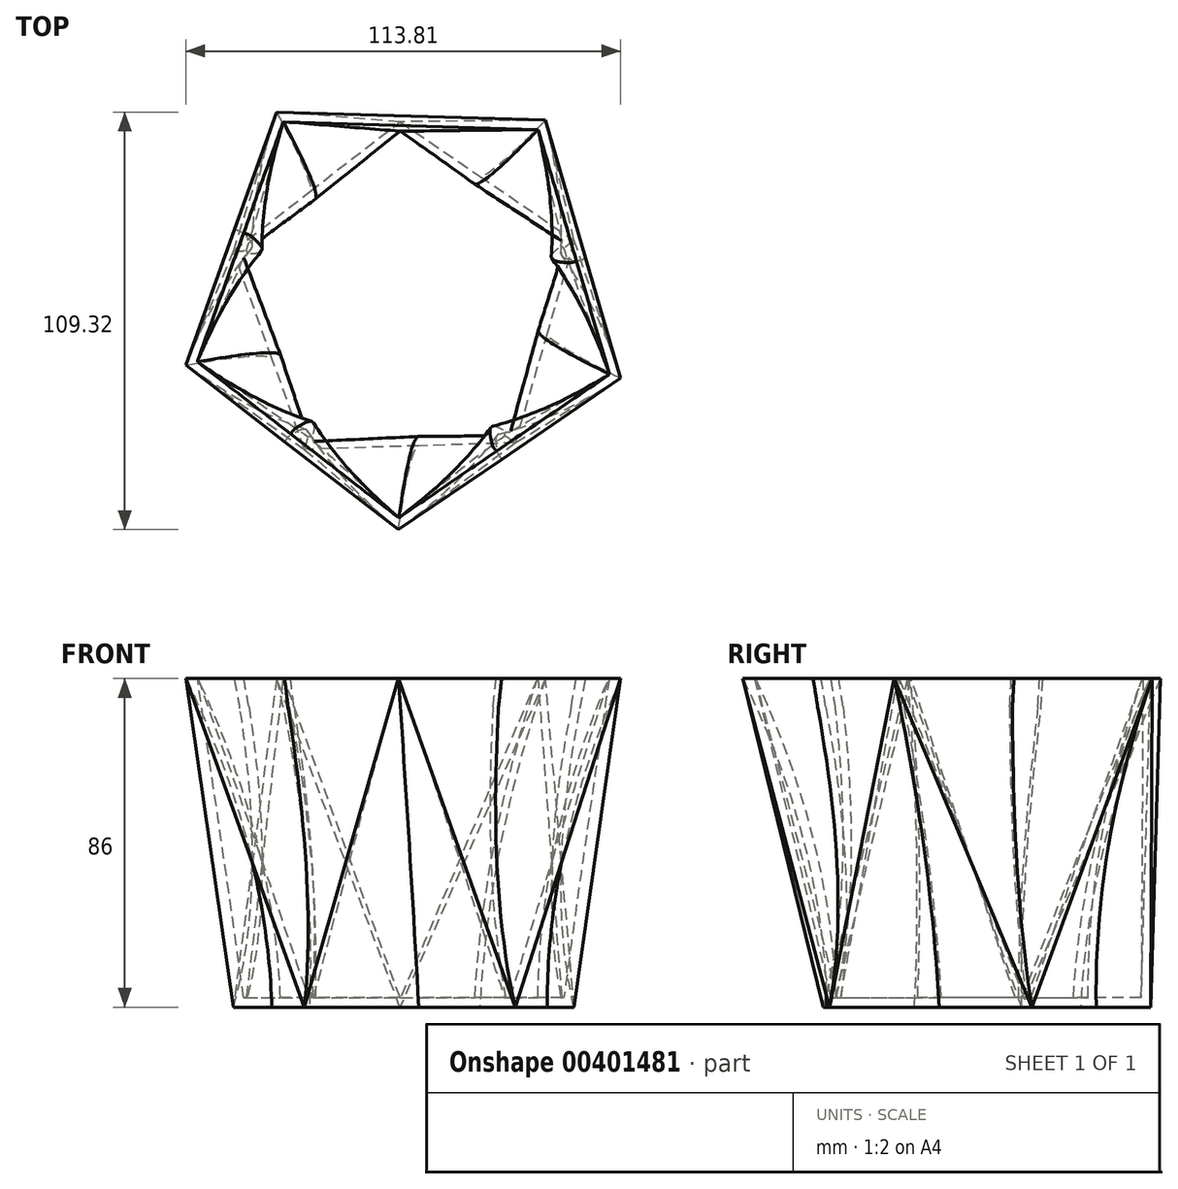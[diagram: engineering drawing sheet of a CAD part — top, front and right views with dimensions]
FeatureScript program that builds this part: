
annotation { "Feature Type Name" : "Feature", "Feature Type Description" : "" }
export const myFeature = defineFeature(function(context is Context, id is Id, definition is map)
    precondition{}
    {
        {
            var Q0;
            Q0=qCreatedBy(makeId("Top.planeOp"),FACE);
            var sketch = newSketch(context, id + "F0", { "sketchPlane" : qUnion([Q0])});
            skCircle(sketch, "E0.cCircle", {"center": v(0, 0) * mm, "radius": 37.98 * mm, "construction": true});
            skLineSegment(sketch, "E0.0", {"start": v(-1.43, 46.92) * mm, "end": v(44.18, 15.86) * mm});
            skLineSegment(sketch, "E0.1", {"start": v(44.18, 15.86) * mm, "end": v(28.73, -37.12) * mm});
            skLineSegment(sketch, "E0.2", {"start": v(28.73, -37.12) * mm, "end": v(-26.42, -38.8) * mm});
            skLineSegment(sketch, "E0.3", {"start": v(-26.42, -38.8) * mm, "end": v(-45.06, 13.14) * mm});
            skLineSegment(sketch, "E0.4", {"start": v(-45.06, 13.14) * mm, "end": v(-1.43, 46.92) * mm});
            skPoint(sketch, "E0.0.midPoint", {"position": v(21.38, 31.39) * mm});
            skSolve(sketch);
        }
        {
            var Q0;
            Q0=qCreatedBy(makeId("Top.planeOp"),FACE);
            cPlane(context, id + "F1", {"entities" : qUnion([Q0]), "cplaneType" : CPlaneType.OFFSET, "offset" : 86 * mm, "width" : 150 * mm, "height" : 150 * mm});
        }
        {
            var Q0;
            Q0=qCreatedBy(id+"F1.planeOp",FACE);
            var sketch = newSketch(context, id + "F2", { "sketchPlane" : qUnion([Q0])});
            skCircle(sketch, "E1.cCircle", {"center": v(0, 0) * mm, "radius": 48.43 * mm, "construction": true});
            skLineSegment(sketch, "E1.0", {"start": v(36.65, 47.34) * mm, "end": v(56.34, -20.23) * mm});
            skLineSegment(sketch, "E1.1", {"start": v(56.34, -20.23) * mm, "end": v(-1.82, -59.84) * mm});
            skLineSegment(sketch, "E1.2", {"start": v(-1.82, -59.84) * mm, "end": v(-57.47, -16.75) * mm});
            skLineSegment(sketch, "E1.3", {"start": v(-57.47, -16.75) * mm, "end": v(-33.7, 49.48) * mm});
            skLineSegment(sketch, "E1.4", {"start": v(-33.7, 49.48) * mm, "end": v(36.65, 47.34) * mm});
            skPoint(sketch, "E1.0.midPoint", {"position": v(46.5, 13.55) * mm});
            skSolve(sketch);
        }
        {
            var Q0;
            Q0=makeQuery(id+"F0.imprint","IMPRINT",FACE,{"disambiguationData":[TD([[makeQuery(id+"F0.imprint","IMPRINT",EDGE,{"derivedFrom":sQuery(id+"F0.wireOp",EDGE,"E0.0")}),-1.0]])]});
            var Q1;
            Q1=makeQuery(id+"F2.imprint","IMPRINT",FACE,{"disambiguationData":[TD([[makeQuery(id+"F2.imprint","IMPRINT",EDGE,{"derivedFrom":sQuery(id+"F2.wireOp",EDGE,"E1.0")}),-1.0]])]});
            loft(context, id + "F3", {"sheetProfilesArray" : [{ "sheetProfileEntities" : qUnion([Q0]) }, { "sheetProfileEntities" : qUnion([Q1]) }]});
        }
        {
            var Q1;
            Q1=makeQuery(id+"F3.opLoft","CAP_FACE",FACE,{"disambiguationData":[OSD([makeQuery(id+"F2.imprint","IMPRINT",FACE,{"disambiguationData":[TD([[makeQuery(id+"F2.imprint","IMPRINT",EDGE,{"derivedFrom":sQuery(id+"F2.wireOp",EDGE,"E1.0")}),-1.0]])]})])],"isStart":true});
            var Q2;
            Q2=makeQuery(id+"F3.opLoft","CAP_FACE",FACE,{"disambiguationData":[OSD([makeQuery(id+"F0.imprint","IMPRINT",FACE,{"disambiguationData":[TD([[makeQuery(id+"F0.imprint","IMPRINT",EDGE,{"derivedFrom":sQuery(id+"F0.wireOp",EDGE,"E0.0")}),-1.0]])]})])],"isStart":true});
            var Q3;
            Q3=makeQuery(id+"F3.opLoft","MID_CAP_VERTEX",VERTEX,{"disambiguationData":[OSD([sQuery(id+"F2.wireOp",EDGE,"E1.1"),sQuery(id+"F2.wireOp",EDGE,"E1.2")])],"capPos":1.0});
            var Q4;
            Q4=makeQuery(id+"F3.opLoft","MID_CAP_VERTEX",VERTEX,{"disambiguationData":[OSD([sQuery(id+"F0.wireOp",EDGE,"E0.1"),sQuery(id+"F0.wireOp",EDGE,"E0.2")])],"capPos":0.0});
            loft(context, id + "F4", {"sheetProfilesArray" : [{ "sheetProfileEntities" : qUnion([Q1]) }, { "sheetProfileEntities" : qUnion([Q2]) }], "matchConnections" : true, "connections" : [{ "connectionEntities" : qUnion([Q3, Q4]), "connectionEdgeQueries" : qUnion([]), "connectionEdgeParameters" : [] }]});
        }
        {
            var Q0;
            Q0=makeQuery(id+"F3.opLoft","MID_CAP_VERTEX",VERTEX,{"disambiguationData":[OSD([sQuery(id+"F2.wireOp",EDGE,"E1.0"),sQuery(id+"F2.wireOp",EDGE,"E1.4")])],"capPos":1.0});
            var Q1;
            Q1=makeQuery(id+"F3.opLoft","MID_CAP_VERTEX",VERTEX,{"disambiguationData":[OSD([sQuery(id+"F2.wireOp",EDGE,"E1.3"),sQuery(id+"F2.wireOp",EDGE,"E1.4")])],"capPos":1.0});
            var Q2;
            Q2=makeQuery(id+"F3.opLoft","MID_CAP_VERTEX",VERTEX,{"disambiguationData":[OSD([sQuery(id+"F0.wireOp",EDGE,"E0.0"),sQuery(id+"F0.wireOp",EDGE,"E0.4")])],"capPos":0.0});
            cPlane(context, id + "F5", {"entities" : qUnion([Q0, Q1, Q2]), "cplaneType" : CPlaneType.THREE_POINT, "offset" : 25 * mm, "width" : 150 * mm, "height" : 150 * mm});
        }
        {
            var Q0;
            Q0=qCreatedBy(id+"F5.planeOp",FACE);
            var sketch = newSketch(context, id + "F6", { "sketchPlane" : qUnion([Q0])});
            skPoint(sketch, "E2.0", {"position": v(-35.24, 86.85) * mm});
            skPoint(sketch, "E3.0", {"position": v(35.14, 86.9) * mm});
            skPoint(sketch, "E4.0", {"position": v(2.86, 0.86) * mm});
            skLineSegment(sketch, "E5", {"start": v(-35.24, 86.85) * mm, "end": v(35.14, 86.9) * mm});
            skLineSegment(sketch, "E6", {"start": v(2.86, 0.86) * mm, "end": v(-35.24, 86.85) * mm});
            skLineSegment(sketch, "E7", {"start": v(35.14, 86.9) * mm, "end": v(2.86, 0.86) * mm});
            skSolve(sketch);
        }
        {
            var Q0;
            Q0 = qSketchRegion(id + "F6", true);
            extrude(context, id + "F7", {"entities" : qUnion([Q0]), "operationType" : NewBodyOperationType.ADD, "endBound" : BoundingType.UP_TO_NEXT, "oppositeDirection" : true, "depth" : 25 * mm});
        }
        {
            var Q0;
            Q0=makeQuery(id+"F3.opLoft","CAP_FACE",FACE,{"disambiguationData":[OSD([makeQuery(id+"F2.imprint","IMPRINT",FACE,{"disambiguationData":[TD([[makeQuery(id+"F2.imprint","IMPRINT",EDGE,{"derivedFrom":sQuery(id+"F2.wireOp",EDGE,"E1.0")}),-1.0]])]})])],"isStart":true});
            shell(context, id + "F8", {"entities" : qUnion([Q0]), "thickness" : 2.5 * mm});
        }
    });
